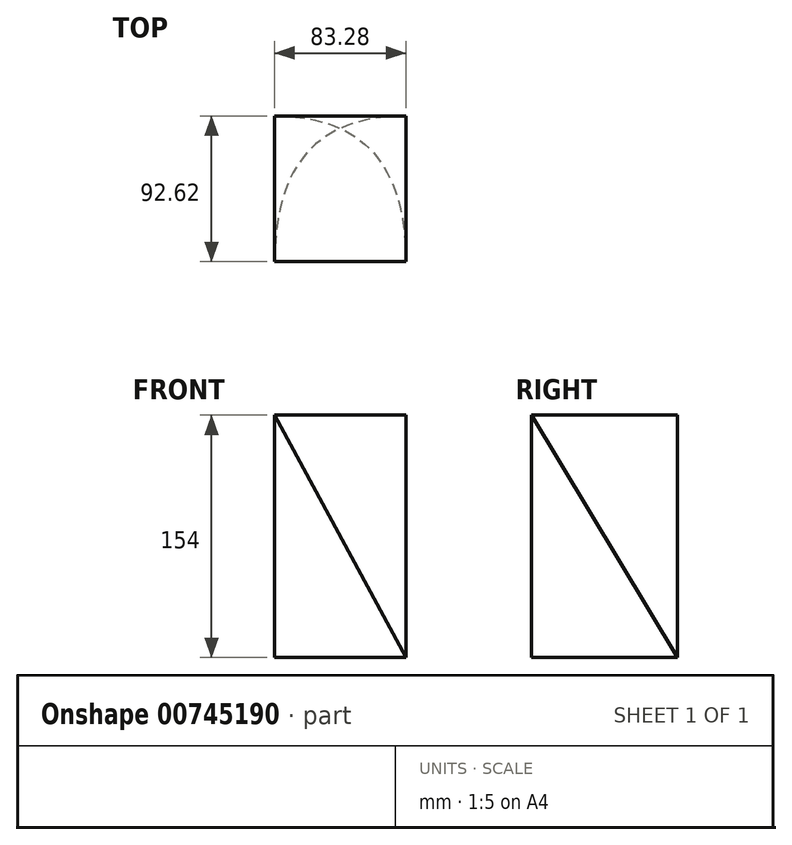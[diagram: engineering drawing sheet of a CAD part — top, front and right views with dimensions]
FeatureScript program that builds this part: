
annotation { "Feature Type Name" : "Feature", "Feature Type Description" : "" }
export const myFeature = defineFeature(function(context is Context, id is Id, definition is map)
    precondition{}
    {
        {
            var Q0;
            Q0=qCreatedBy(makeId("Top.planeOp"),FACE);
            cPlane(context, id + "F0", {"entities" : qUnion([Q0]), "cplaneType" : CPlaneType.OFFSET, "offset" : 154 * mm, "width" : 150 * mm, "height" : 150 * mm});
        }
        {
            var Q0;
            Q0=qCreatedBy(makeId("Top.planeOp"),FACE);
            var sketch = newSketch(context, id + "F1", { "sketchPlane" : qUnion([Q0])});
            skLineSegment(sketch, "E0.bottom", {"start": v(-41.64, -46.31) * mm, "end": v(41.64, -46.31) * mm});
            skLineSegment(sketch, "E0.top", {"start": v(-41.64, 46.31) * mm, "end": v(41.64, 46.31) * mm});
            skLineSegment(sketch, "E0.left", {"start": v(-41.64, -46.31) * mm, "end": v(-41.64, 46.31) * mm});
            skLineSegment(sketch, "E0.right", {"start": v(41.64, -46.31) * mm, "end": v(41.64, 46.31) * mm});
            skPoint(sketch, "E0.middle", {"position": v(0, 0) * mm});
            skSolve(sketch);
        }
        {
            var Q0;
            Q0=qCreatedBy(id+"F0.planeOp",FACE);
            var sketch = newSketch(context, id + "F2", { "sketchPlane" : qUnion([Q0])});
            skLineSegment(sketch, "E1.0", {"start": v(-41.64, -46.31) * mm, "end": v(-41.64, 46.31) * mm});
            skLineSegment(sketch, "E2.0", {"start": v(-41.64, 46.31) * mm, "end": v(41.64, 46.31) * mm});
            skLineSegment(sketch, "E3.0", {"start": v(41.64, -46.31) * mm, "end": v(41.64, 46.31) * mm});
            skLineSegment(sketch, "E4.0", {"start": v(-41.64, -46.31) * mm, "end": v(41.64, -46.31) * mm});
            skSolve(sketch);
        }
        {
            var Q0;
            Q0=makeQuery(id+"F2.imprint","IMPRINT",FACE,{"disambiguationData":[TD([[makeQuery(id+"F2.imprint","IMPRINT",EDGE,{"derivedFrom":sQuery(id+"F2.wireOp",EDGE,"E1.0")}),-1.0]])]});
            var Q1;
            Q1=makeQuery(id+"F1.imprint","IMPRINT",FACE,{"disambiguationData":[TD([[makeQuery(id+"F1.imprint","IMPRINT",EDGE,{"derivedFrom":sQuery(id+"F1.wireOp",EDGE,"E0.bottom")}),1.0]])]});
            var Q2;
            Q2=sQuery(id+"F2.wireOp",VERTEX,"E3.0.start");
            var Q3;
            Q3=sQuery(id+"F1.wireOp",VERTEX,"E0.right.end");
            loft(context, id + "F3", {"sheetProfilesArray" : [{ "sheetProfileEntities" : qUnion([Q0]) }, { "sheetProfileEntities" : qUnion([Q1]) }], "matchConnections" : true, "connections" : [{ "connectionEntities" : qUnion([Q2, Q3]), "connectionEdgeQueries" : qUnion([]), "connectionEdgeParameters" : [] }]});
        }
    });
